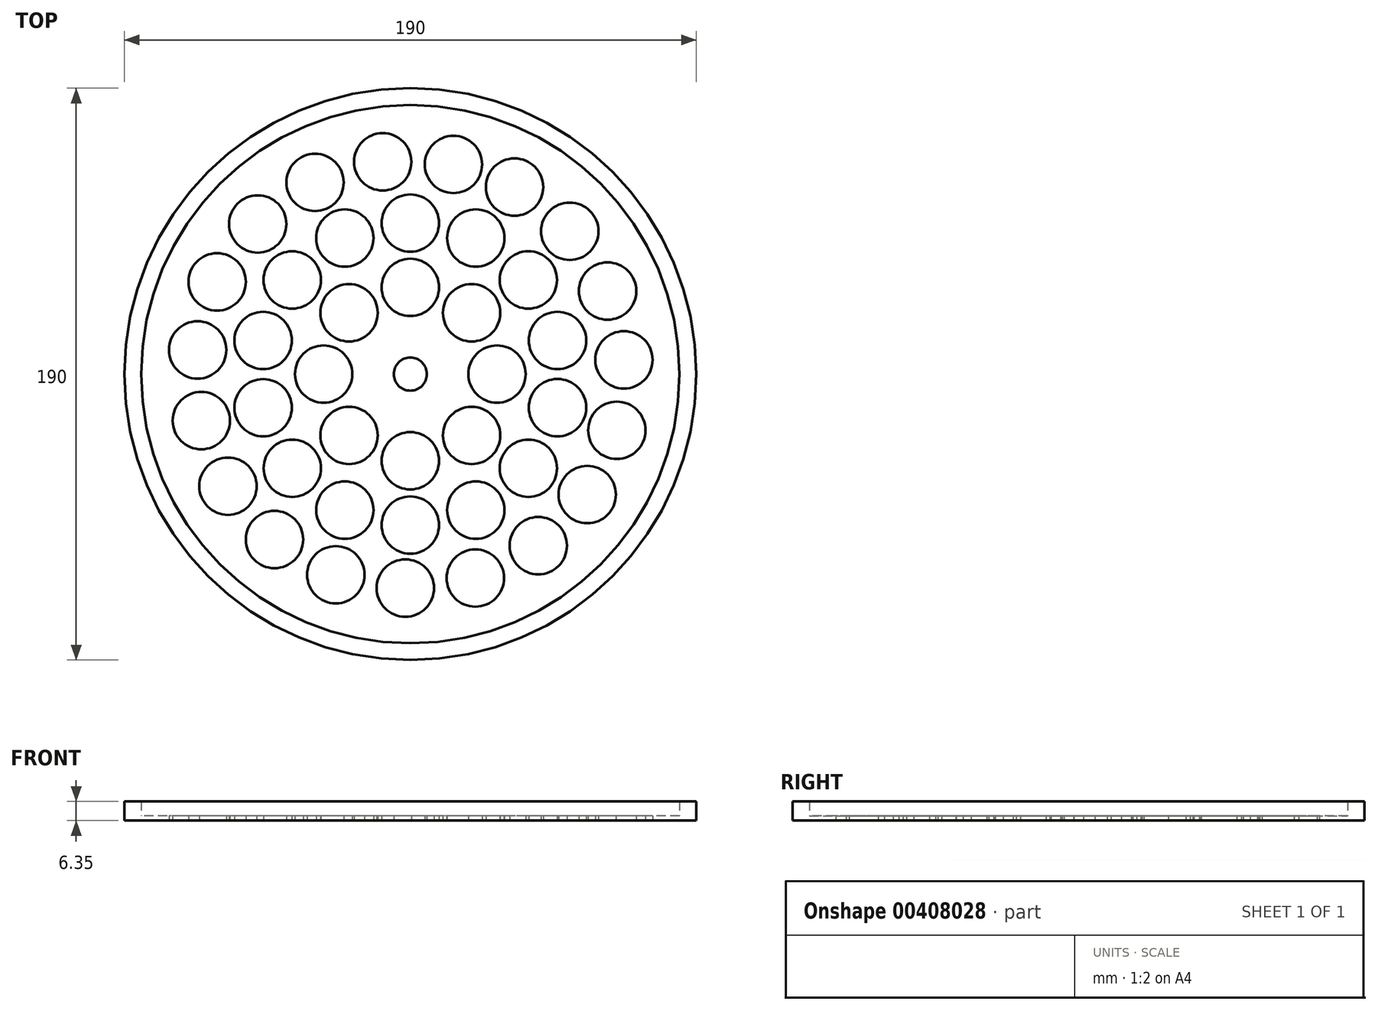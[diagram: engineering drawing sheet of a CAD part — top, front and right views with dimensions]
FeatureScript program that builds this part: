
annotation { "Feature Type Name" : "Feature", "Feature Type Description" : "" }
export const myFeature = defineFeature(function(context is Context, id is Id, definition is map)
    precondition{}
    {
        {
            var Q0;
            Q0=qCreatedBy(makeId("Top.planeOp"),FACE);
            var sketch = newSketch(context, id + "F0", { "sketchPlane" : qUnion([Q0])});
            skCircle(sketch, "E0", {"center": v(0, 0) * mm, "radius": 95 * mm});
            skCircle(sketch, "E1", {"center": v(0, 0) * mm, "radius": 40 * mm, "construction": true});
            skCircle(sketch, "E2", {"center": v(0, 0) * mm, "radius": 80 * mm, "construction": true});
            skCircle(sketch, "E3", {"center": v(0, 28.8) * mm, "radius": 9.53 * mm});
            skCircle(sketch, "E4", {"center": v(-48.9, -11.17) * mm, "radius": 9.53 * mm});
            skCircle(sketch, "E5", {"center": v(39.22, -31.28) * mm, "radius": 9.53 * mm});
            skCircle(sketch, "E6", {"center": v(52.97, 47.45) * mm, "radius": 9.53 * mm});
            skCircle(sketch, "E7", {"center": v(65.55, 27.6) * mm, "radius": 9.53 * mm});
            skCircle(sketch, "E8", {"center": v(-39.22, -31.28) * mm, "radius": 9.53 * mm});
            skCircle(sketch, "E9", {"center": v(-39.22, 31.27) * mm, "radius": 9.53 * mm});
            skCircle(sketch, "E10", {"center": v(34.6, 62.13) * mm, "radius": 9.53 * mm});
            skCircle(sketch, "E11", {"center": v(-50.7, 49.88) * mm, "radius": 9.53 * mm});
            skCircle(sketch, "E12", {"center": v(-1.66, -71.1) * mm, "radius": 9.53 * mm});
            skCircle(sketch, "E13", {"center": v(-60.59, -37.24) * mm, "radius": 9.53 * mm});
            skCircle(sketch, "E14", {"center": v(-48.9, 11.16) * mm, "radius": 9.53 * mm});
            skCircle(sketch, "E15", {"center": v(21.77, -45.2) * mm, "radius": 9.53 * mm});
            skCircle(sketch, "E16", {"center": v(0, -50.16) * mm, "radius": 9.53 * mm});
            skCircle(sketch, "E17", {"center": v(-21.76, -45.2) * mm, "radius": 9.53 * mm});
            skCircle(sketch, "E18", {"center": v(-31.67, 63.68) * mm, "radius": 9.53 * mm});
            skCircle(sketch, "E19", {"center": v(-64.19, 30.62) * mm, "radius": 9.53 * mm});
            skCircle(sketch, "E20", {"center": v(20.36, 20.36) * mm, "radius": 9.53 * mm});
            skCircle(sketch, "E21", {"center": v(70.96, 4.71) * mm, "radius": 9.53 * mm});
            skCircle(sketch, "E22", {"center": v(68.62, -18.68) * mm, "radius": 9.53 * mm});
            skCircle(sketch, "E23", {"center": v(58.78, -40.03) * mm, "radius": 9.53 * mm});
            skCircle(sketch, "E24", {"center": v(-69.42, -15.45) * mm, "radius": 9.53 * mm});
            skCircle(sketch, "E25", {"center": v(-70.67, 8.02) * mm, "radius": 9.53 * mm});
            skCircle(sketch, "E26", {"center": v(-21.77, 45.2) * mm, "radius": 9.53 * mm});
            skCircle(sketch, "E27", {"center": v(21.6, -67.76) * mm, "radius": 9.53 * mm});
            skCircle(sketch, "E28", {"center": v(42.52, -57.01) * mm, "radius": 9.53 * mm});
            skCircle(sketch, "E29", {"center": v(-45.14, -54.96) * mm, "radius": 9.53 * mm});
            skCircle(sketch, "E30", {"center": v(-28.8, 0) * mm, "radius": 9.53 * mm});
            skCircle(sketch, "E31", {"center": v(20.36, -20.36) * mm, "radius": 9.53 * mm});
            skCircle(sketch, "E32", {"center": v(-20.36, -20.36) * mm, "radius": 9.53 * mm});
            skCircle(sketch, "E33", {"center": v(-20.36, 20.36) * mm, "radius": 9.53 * mm});
            skCircle(sketch, "E34", {"center": v(-24.75, -66.67) * mm, "radius": 9.53 * mm});
            skCircle(sketch, "E35", {"center": v(39.22, 31.28) * mm, "radius": 9.53 * mm});
            skCircle(sketch, "E36", {"center": v(0, 50.17) * mm, "radius": 9.53 * mm});
            skCircle(sketch, "E37", {"center": v(48.9, -11.16) * mm, "radius": 9.53 * mm});
            skCircle(sketch, "E38", {"center": v(48.9, 11.16) * mm, "radius": 9.53 * mm});
            skCircle(sketch, "E39", {"center": v(21.77, 45.2) * mm, "radius": 9.53 * mm});
            skCircle(sketch, "E40", {"center": v(0, -28.8) * mm, "radius": 9.53 * mm});
            skCircle(sketch, "E41", {"center": v(28.8, 0) * mm, "radius": 9.53 * mm});
            skCircle(sketch, "E42", {"center": v(0, 0) * mm, "radius": 5.5 * mm});
            skCircle(sketch, "E43", {"center": v(0, 0) * mm, "radius": 28.8 * mm, "construction": true});
            skCircle(sketch, "E44", {"center": v(0, 0) * mm, "radius": 50.17 * mm, "construction": true});
            skCircle(sketch, "E45", {"center": v(0, 0) * mm, "radius": 71.12 * mm, "construction": true});
            skCircle(sketch, "E46", {"center": v(0, 0) * mm, "radius": 60 * mm, "construction": true});
            skCircle(sketch, "E47", {"center": v(-9.18, 70.53) * mm, "radius": 9.53 * mm});
            skCircle(sketch, "E48", {"center": v(14.32, 69.66) * mm, "radius": 9.53 * mm});
            skCircle(sketch, "E49", {"center": v(0, 0) * mm, "radius": 89.4 * mm});
            skSolve(sketch);
        }
        {
            var Q0;
            Q0=makeQuery(id+"F0.imprint","IMPRINT",FACE,{"disambiguationData":[TD([[makeQuery(id+"F0.imprint","IMPRINT",EDGE,{"derivedFrom":sQuery(id+"F0.wireOp",EDGE,"E3")}),-1.0]])]});
            extrude(context, id + "F1", {"entities" : qUnion([Q0]), "depth" : 1.52 * mm, "offsetDistance" : 25.4 * mm});
        }
        {
            var Q0;
            Q0=makeQuery(id+"F0.imprint","IMPRINT",FACE,{"disambiguationData":[TD([[makeQuery(id+"F0.imprint","IMPRINT",EDGE,{"derivedFrom":sQuery(id+"F0.wireOp",EDGE,"E0")}),1.0]])]});
            extrude(context, id + "F2", {"entities" : qUnion([Q0]), "operationType" : NewBodyOperationType.ADD, "depth" : 6.35 * mm, "offsetDistance" : 25.4 * mm});
        }
    });
